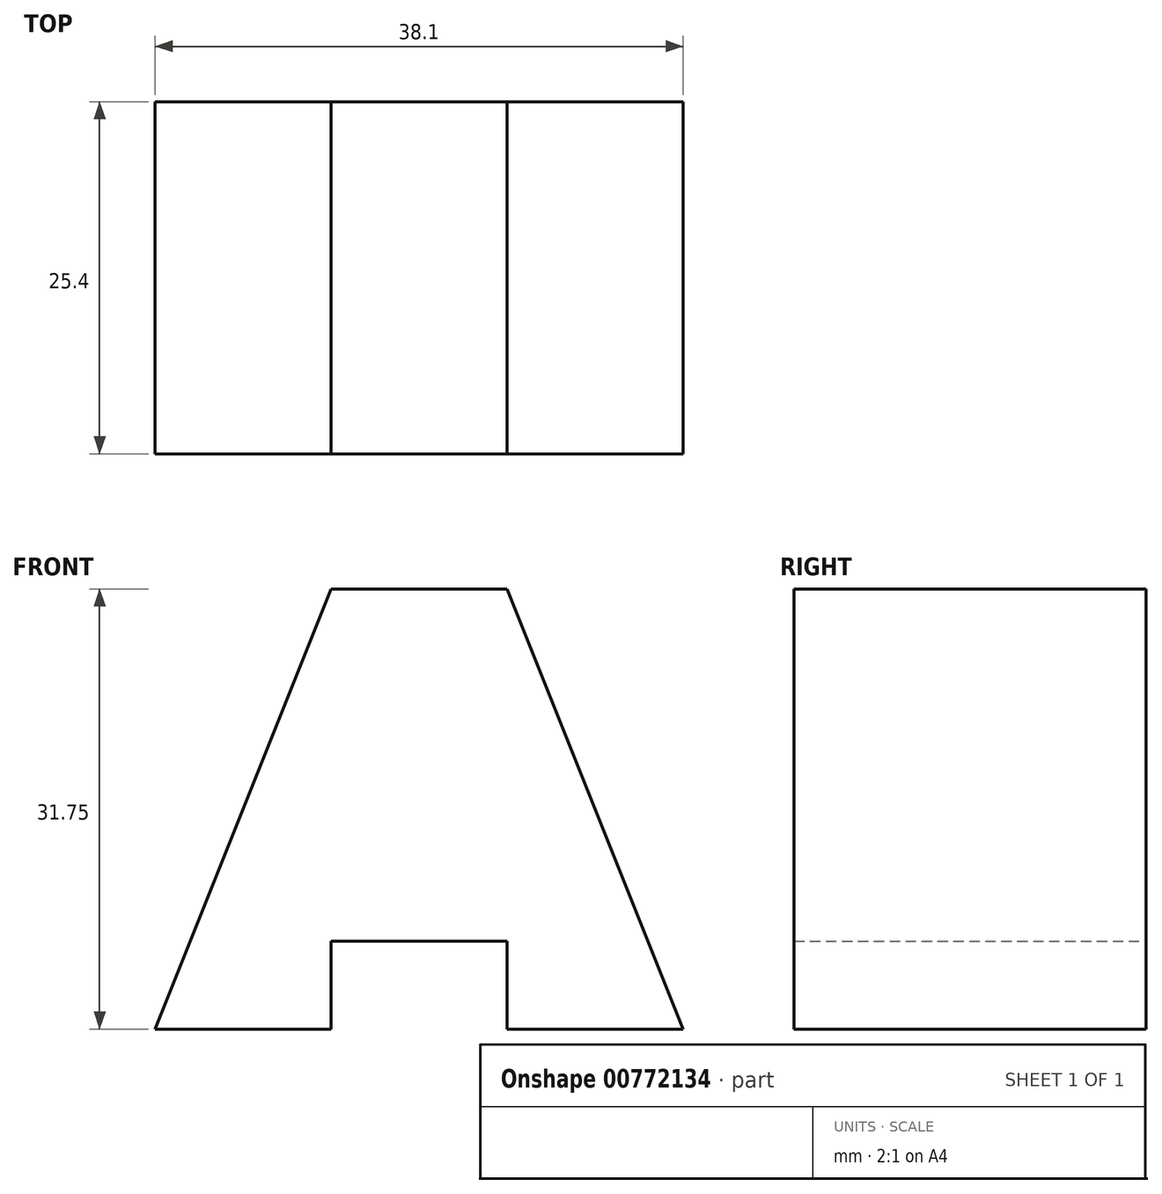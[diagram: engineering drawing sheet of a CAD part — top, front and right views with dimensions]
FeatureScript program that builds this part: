
annotation { "Feature Type Name" : "Feature", "Feature Type Description" : "" }
export const myFeature = defineFeature(function(context is Context, id is Id, definition is map)
    precondition{}
    {
        {
            var Q0;
            Q0=qCreatedBy(makeId("Front.planeOp"),FACE);
            var sketch = newSketch(context, id + "F0", { "sketchPlane" : qUnion([Q0])});
            skLineSegment(sketch, "E0", {"start": v(0, 0) * mm, "end": v(12.7, 0) * mm});
            skLineSegment(sketch, "E1", {"start": v(12.7, 0) * mm, "end": v(12.7, 6.35) * mm});
            skLineSegment(sketch, "E2", {"start": v(12.7, 6.35) * mm, "end": v(25.4, 6.35) * mm});
            skLineSegment(sketch, "E3", {"start": v(25.4, 6.35) * mm, "end": v(25.4, 0) * mm});
            skLineSegment(sketch, "E4", {"start": v(25.4, 0) * mm, "end": v(38.1, 0) * mm});
            skLineSegment(sketch, "E5", {"start": v(38.1, 0) * mm, "end": v(38.1, 31.75) * mm});
            skLineSegment(sketch, "E6", {"start": v(38.1, 31.75) * mm, "end": v(0, 31.75) * mm});
            skLineSegment(sketch, "E7", {"start": v(0, 31.75) * mm, "end": v(0, 0) * mm});
            skSolve(sketch);
        }
        {
            var Q0;
            Q0=makeQuery(id+"F0.imprint","IMPRINT",FACE,{"disambiguationData":[TD([[makeQuery(id+"F0.imprint","IMPRINT",EDGE,{"derivedFrom":sQuery(id+"F0.wireOp",EDGE,"E0")}),1.0]])]});
            extrude(context, id + "F1", {"entities" : qUnion([Q0]), "depth" : 25.4 * mm, "offsetDistance" : 25.4 * mm});
        }
        {
            var Q0;
            Q0=makeQuery(id+"F1.opExtrude","CAP_FACE",FACE,{"disambiguationData":[OSD([sQuery(id+"F0.wireOp",EDGE,"E0"),sQuery(id+"F0.wireOp",EDGE,"E1"),sQuery(id+"F0.wireOp",EDGE,"E2"),sQuery(id+"F0.wireOp",EDGE,"E3"),sQuery(id+"F0.wireOp",EDGE,"E4"),sQuery(id+"F0.wireOp",EDGE,"E5"),sQuery(id+"F0.wireOp",EDGE,"E6"),sQuery(id+"F0.wireOp",EDGE,"E7")])],"isStart":false});
            var sketch = newSketch(context, id + "F2", { "sketchPlane" : qUnion([Q0])});
            skLineSegment(sketch, "E8", {"start": v(38.1, 0) * mm, "end": v(25.4, 31.75) * mm});
            skLineSegment(sketch, "E9", {"start": v(25.4, 31.75) * mm, "end": v(12.7, 31.75) * mm});
            skLineSegment(sketch, "E10", {"start": v(12.7, 31.75) * mm, "end": v(0, 0) * mm});
            skSolve(sketch);
        }
        {
            var Q0;
            {var subQ0=sQuery(id+"F2.wireOp",EDGE,"E8");Q0=makeQuery(id+"F2.imprint","IMPRINT",FACE,{"disambiguationData":[TD([[makeQuery(id+"F2.imprint","IMPRINT",EDGE,{"derivedFrom":subQ0}),-1.0]])]});}
            extrude(context, id + "F3", {"entities" : qUnion([Q0]), "operationType" : NewBodyOperationType.REMOVE, "oppositeDirection" : true, "depth" : 25.4 * mm, "offsetDistance" : 25.4 * mm});
        }
        {
            var Q0;
            Q0=makeQuery(id+"F1.opExtrude","CAP_FACE",FACE,{"disambiguationData":[OSD([sQuery(id+"F0.wireOp",EDGE,"E0"),sQuery(id+"F0.wireOp",EDGE,"E1"),sQuery(id+"F0.wireOp",EDGE,"E2"),sQuery(id+"F0.wireOp",EDGE,"E3"),sQuery(id+"F0.wireOp",EDGE,"E4"),sQuery(id+"F0.wireOp",EDGE,"E5"),sQuery(id+"F0.wireOp",EDGE,"E6"),sQuery(id+"F0.wireOp",EDGE,"E7")])],"isStart":false});
            var sketch = newSketch(context, id + "F4", { "sketchPlane" : qUnion([Q0])});
            skLineSegment(sketch, "E11", {"start": v(25.4, 31.75) * mm, "end": v(12.7, 31.75) * mm});
            skLineSegment(sketch, "E12", {"start": v(12.7, 31.75) * mm, "end": v(0, 0) * mm});
            skSolve(sketch);
        }
        {
            var Q0;
            {var subQ0=sQuery(id+"F4.wireOp",EDGE,"E12");Q0=makeQuery(id+"F4.imprint","IMPRINT",FACE,{"disambiguationData":[TD([[makeQuery(id+"F4.imprint","IMPRINT",EDGE,{"derivedFrom":subQ0}),-1.0]])]});}
            extrude(context, id + "F5", {"entities" : qUnion([Q0]), "operationType" : NewBodyOperationType.REMOVE, "oppositeDirection" : true, "depth" : 25.4 * mm, "offsetDistance" : 25.4 * mm});
        }
    });
